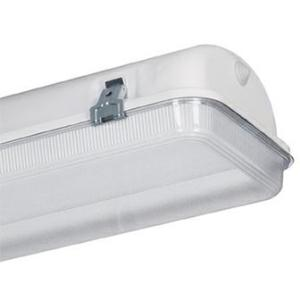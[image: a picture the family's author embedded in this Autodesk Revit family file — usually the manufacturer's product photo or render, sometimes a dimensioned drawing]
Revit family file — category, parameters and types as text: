
# Revit family: 3f_filippi_-_beta_i3f_75_pc_ampio_3f_filippi_-_55598_-_i3f_led_752x24w_ampio_l1265
name_source: partatom
category: Lighting Fixtures
units: mm (PartAtom-declared; Revit-internal decimal feet)

## family parameters
Cut with Voids When Loaded = No
Host = Face
Light Source = No
Part Type = Normal
Room Calculation Point = No
Round Connector Dimension = Use Diameter
Shared = No

## types (1)
- 3F Filippi - Beta i3F 75 PC Ampio (1 x LED, 7471 lm, 54 W, 4000 K)
    Apparent Load = 54 VA
    Approval mark = ENEC
    CIE Flux Codes = 52 82 96 97 100
    Color Rendering = 80
    Color Temperature = 4000 K
    Control Gear = Electronic ballast
    Default Elevation = 1800 mm
    Description = ILLUMINOTECHNICAL
Luminous efficiency 100% (DLOR 97%, ULOR 3%).
Initial luminous flux of the luminaire 7471 lm.
Wide symmetric distribution.
Installation Interdistance Transv.D = 1.27 x hu - Long.D = 1.26 x hu.
Tabular UGR (CIE 117 - 4H-8H; S=0.25H; 70/50/20): RUG 20.4 - 22.2.
Beam angle: 92° - 100°.
Luminous efficacy 138 lm/W.
Lifetime (L93/B10): 30000 h. (tq+25°C)
Lifetime (L90/B10): 50000 h. (tq+25°C)
Lifetime (L85/B10): 80000 h. (tq+25°C)
Lifetime (L80/B10): 100000 h. (tq+25°C)
Lifetime (L85/B10): 50000 h. (tq+35°C)
Sudden decreased luminous flux after 50000 hours: 0% (C0).
Photobiological safety in compliance with IEC/TR 62778: RG0 risk exempt, (IEC 62471).
In compliance with IEC/EN 62722-2-1 - IEC/EN 62717 standards.

SOURCE
2 linear LED modules 24W/840.
Energy efficiency class (UE 2019/2020 - UE 2019/2015): D.
CIE 13.3 Colour rendering index: CRI >80 (R9 <50%).
IES TM-30 Fidelity Index: Rf = 84 Rg = 95.
CCT nominal colour temperature 4000 K.
Colour initial tolerance (MacAdam): SDCM 3.

MECHANICAL
Single-piece housing in pressed steel, powder-coated in white epoxy-polyester.
Diffuser in self-extinguishing V2 polycarbonate, photo-engraved interior, UV stabilised, injection moulded, with smooth outer surface, sealing gasket, hinged opening by means of galvanised steel clips.
Wide flow recuperator, oversized, in specular aluminium with superficial titanium-magnesium treatment, non-iridescent.
Gear-tray unit in hot-galvanised steel, painted in white polyester, fixed to the housing by means of "Ribloc" rapid devices in galvanised steel, hinged opening.
Luminaire with limited surface temperature. - D - (EN 60598-2-24)
Dimensions: 1265x235 mm, height 135 mm. Weight 5.7 kg.
IP65 protection degree.
Mechanical strength to impacts IK10 (20 joule).
Glow-wire test resistance 850°C.

ELECTRICAL
Halogen Free electronic wiring 230V-50/60Hz, power factor 0.97, THD <25%, constant output current, SELV, class I, 1 driver.
Power of the luminaire 54 W.
CE - IEC 60598-1 - EN 60598-1.
SAFE FLICKER: PstLM=<1 and SVM=<0.4 (IEC TR 61547-1 and IEC TR 63158), to ensure a more comfortable and safe light.
Luminaire compliant with EN 60598-2-22 for power supply from a centralised emergency system CPSS (Central Power Supply System), not incorporated in the luminaire - high risk areas excluded. The default power and flux are 100% in AC and 100% in DC.
Ambient temperature from -20°C to +35°C.
Temperature class T6 max 85°C.
Relative humidity UR: <85%.

INSTALLATION
Ceiling / Suspended / Wall.
All accessories dedicated to this product are available on the Catalog and on our website www.3F-Filippi.com.

APPLICATIONS
Suitable product for food production plants (HACCP), IFS (Food Version 6), BRC (GSFS Food Version 7).
In industrial environments, stores and dry, dusty indoor environments, subject to occasional water splashes.

WARNING
Fixture not suitable for cold stores with an ambient temperature <0°C and/or relative humidity >85%.
Luminaire designed for disposal/recycling at end-of-life.
Replaceable (LED only) light source by a professional. Replaceable control gear by a professional.
    Height = 135 mm
    Lamp = 1 x LED
    Lamp Light Flux = 7471 lm
    Lamp Power = 54 W
    Lamp count = 1
    Length = 1265 mm
    Lifetime = 50000 h
    Luminous efficacy = 138 lm/W
    Manufacturer = 3F Filippi
    ModVariant = No
    Model = 3F Filippi - 55598 - i3F LED 752x24W AMPIO L1265
    Mounting Place = Ceiling
    Mounting Type = Pendant
    Number of Poles = 1
    OnlyDefault = Yes
    Power Factor = 1
    Product Name = 3F Filippi - Beta i3F 75 PC Ampio
    Product group = pendant luminaire
    ProductGroupID = 9
    Protection Class = Protection class I
    Protection Degree = IP 65
    RLX_Detail_Level = 1
    RLX_Emergency_Light_Flux = 0 lm
    RLX_Emergency_Type = 0
    RLX_Emergency_Type_DB = No
    RlxData = <blob elided: 67921 chars, md5=751401eb>
    Socket = socket
    Standby Power = 0 W
    System Light Flux = 7471 lm
    System Power = 54 W
    Type Comments = Product without accessories
    Type Image = 3ffilippi_55598.jpg
    URL = http://relux.com
    VarID = ---
    Voltage = 0 V
    Weight = 0.00 kg
    Width = 235 mm

## geometry (parser evidence)
native form markers: Blend x4, Sweep x10
no freeform markers — native parametric forms only
